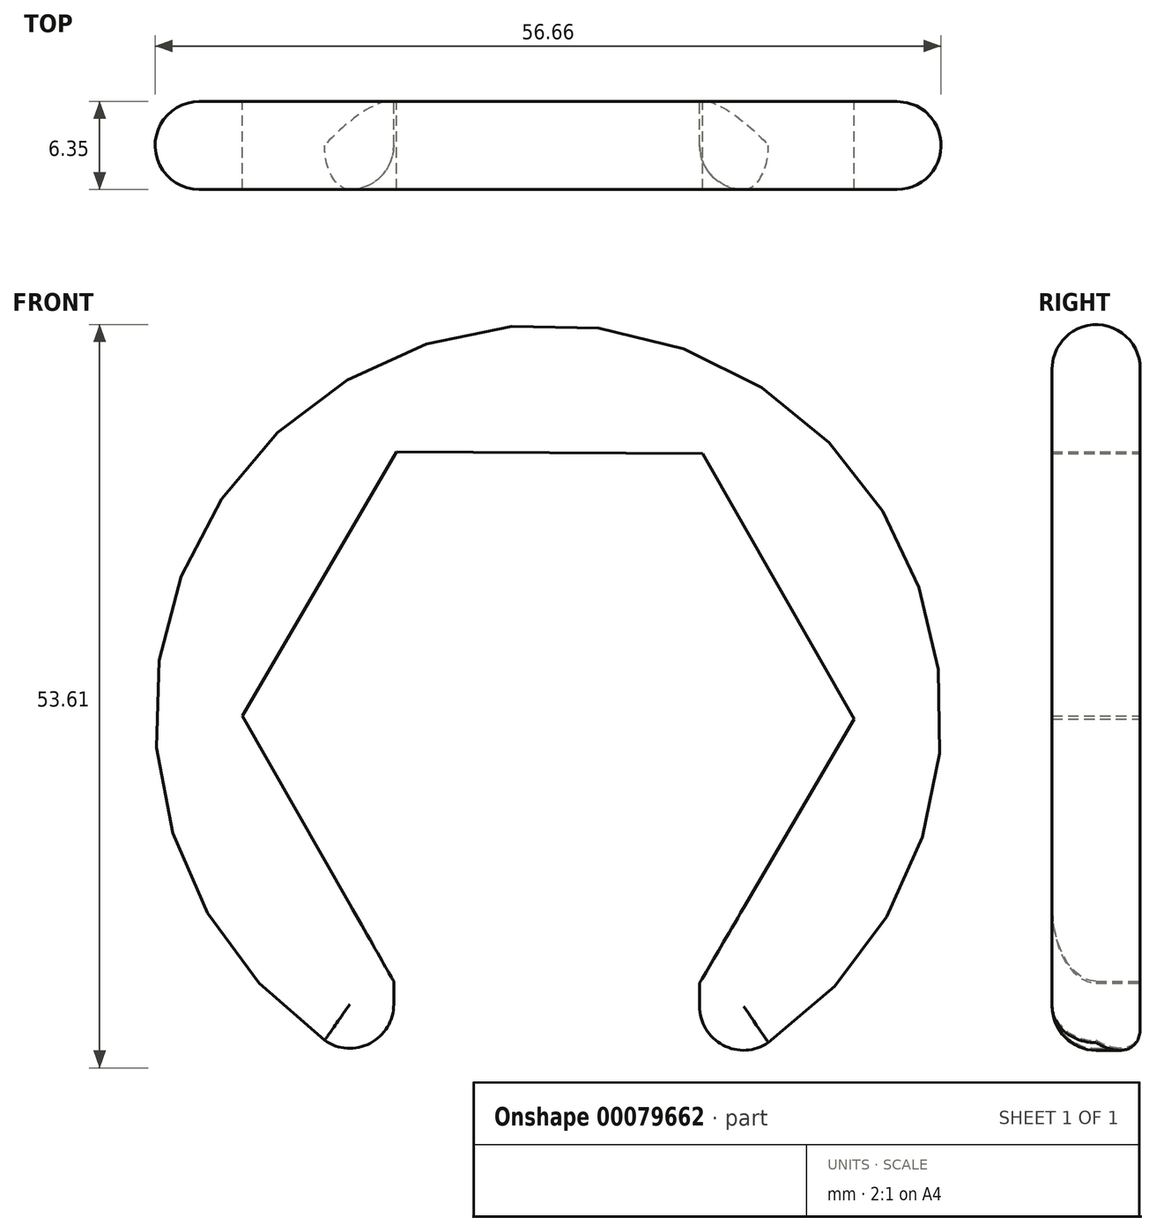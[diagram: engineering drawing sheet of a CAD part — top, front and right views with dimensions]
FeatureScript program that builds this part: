
annotation { "Feature Type Name" : "Feature", "Feature Type Description" : "" }
export const myFeature = defineFeature(function(context is Context, id is Id, definition is map)
    precondition{}
    {
        {
            var Q0;
            Q0=qCreatedBy(makeId("Front.planeOp"),FACE);
            var sketch = newSketch(context, id + "F0", { "sketchPlane" : qUnion([Q0])});
            skArc(sketch, "E0", {"start": v(10.92, -26.14) * mm, "mid": v(0.11, 28.33) * mm, "end": v(-11.13, -26.05) * mm});
            skArc(sketch, "E1.cCircle", {"start": v(16.49, -9.64) * mm, "mid": v(0.1, 19.1) * mm, "end": v(-16.6, -9.46) * mm, "construction": true});
            skLineSegment(sketch, "E1.0", {"start": v(11.13, 19.04) * mm, "end": v(22.05, -0.12) * mm});
            skLineSegment(sketch, "E1.1", {"start": v(22.05, -0.12) * mm, "end": v(10.92, -19.16) * mm});
            skLineSegment(sketch, "E1.3", {"start": v(-11.13, -19.04) * mm, "end": v(-22.05, 0.12) * mm});
            skLineSegment(sketch, "E1.4", {"start": v(-22.05, 0.12) * mm, "end": v(-10.92, 19.16) * mm});
            skLineSegment(sketch, "E1.5", {"start": v(-10.92, 19.16) * mm, "end": v(11.13, 19.04) * mm});
            skPoint(sketch, "E1.0.midPoint", {"position": v(16.6, 9.46) * mm});
            skLineSegment(sketch, "E2", {"start": v(-11.13, -19.04) * mm, "end": v(-11.13, -26.05) * mm});
            skLineSegment(sketch, "E3", {"start": v(10.92, -19.16) * mm, "end": v(10.92, -26.14) * mm});
            skSolve(sketch);
        }
        {
            var Q0;
            Q0 = qSketchRegion(id + "F0", true);
            extrude(context, id + "F1", {"entities" : qUnion([Q0]), "depth" : 6.35 * mm});
        }
        {
            var Q0;
            Q0=makeQuery(id+"F1.opExtrude","CAP_EDGE",EDGE,{"disambiguationData":[OSD([sQuery(id+"F0.wireOp",EDGE,"E0")])],"isStart":false});
            fillet(context, id + "F2", {"entities" : qUnion([Q0]), "radius" : 3.17 * mm, "tangentPropagation" : true, "allowEdgeOverflow" : false});
        }
        {
            var Q0;
            Q0=makeQuery(id+"F1.opExtrude","SWEPT_FACE",FACE,{"disambiguationData":[OSD([sQuery(id+"F0.wireOp",EDGE,"E0")])]});
            fillet(context, id + "F3", {"entities" : qUnion([Q0]), "radius" : 3.17 * mm, "tangentPropagation" : true, "allowEdgeOverflow" : false});
        }
    });
